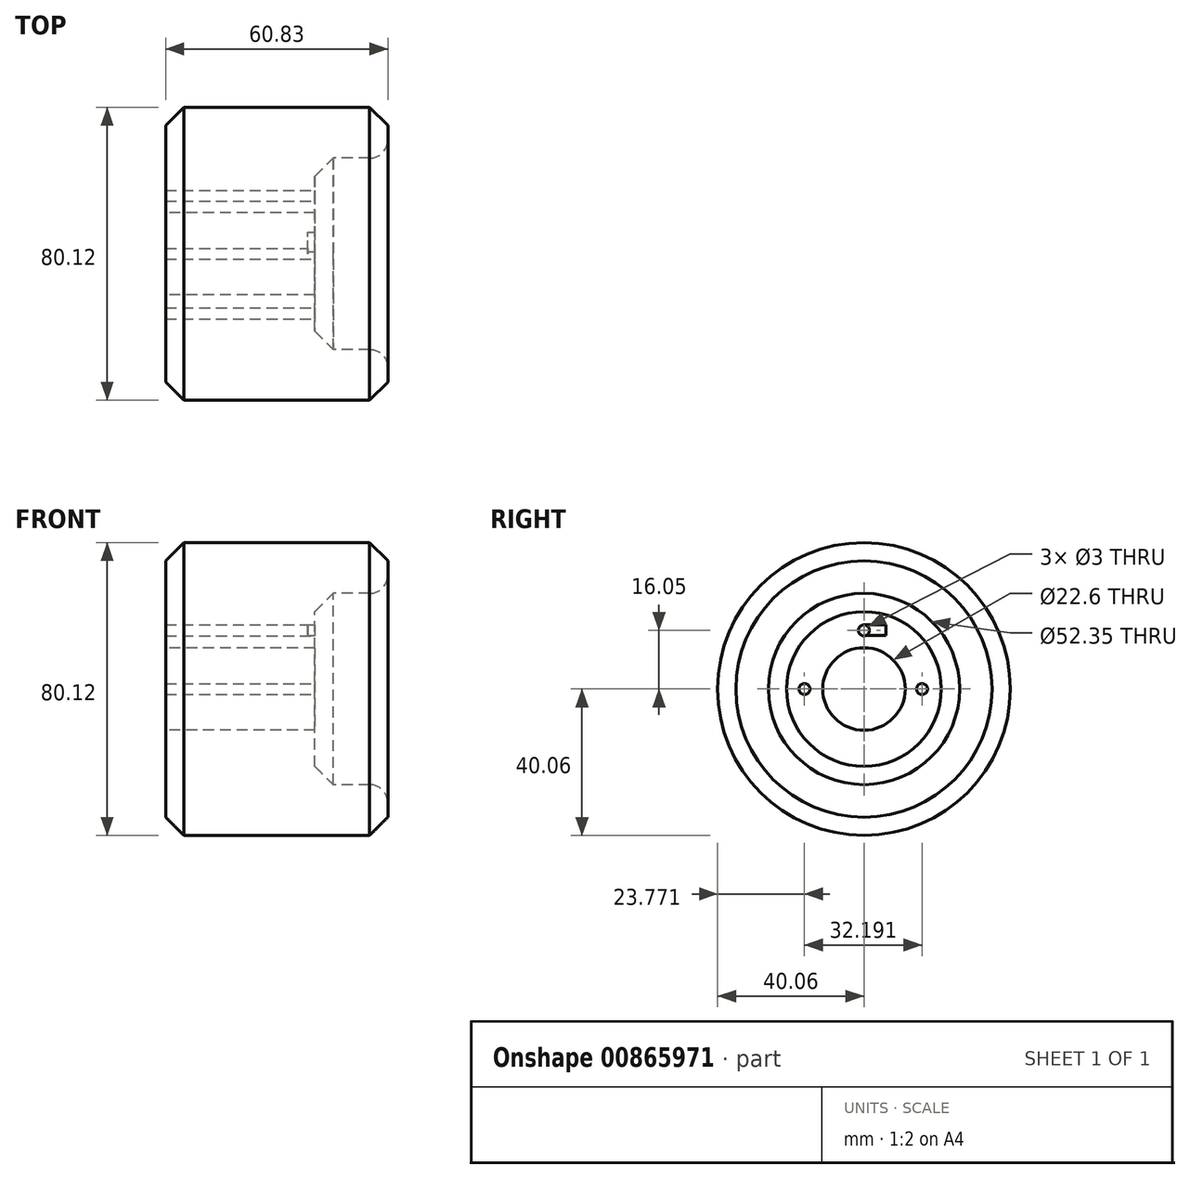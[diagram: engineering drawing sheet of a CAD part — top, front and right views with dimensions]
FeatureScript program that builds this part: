
annotation { "Feature Type Name" : "Feature", "Feature Type Description" : "" }
export const myFeature = defineFeature(function(context is Context, id is Id, definition is map)
    precondition{}
    {
        {
            var Q0;
            Q0=qCreatedBy(makeId("Front.planeOp"),FACE);
            var sketch = newSketch(context, id + "F0", { "sketchPlane" : qUnion([Q0])});
            skLineSegment(sketch, "E0", {"start": v(-75.38, 0) * mm, "end": v(58.63, 0) * mm, "construction": true});
            skLineSegment(sketch, "E1.bottom", {"start": v(-45.99, 40.06) * mm, "end": v(-5.14, 40.06) * mm});
            skLineSegment(sketch, "E1.top", {"start": v(-45.99, 11.3) * mm, "end": v(-5.14, 11.3) * mm});
            skLineSegment(sketch, "E1.left", {"start": v(-45.99, 40.06) * mm, "end": v(-45.99, 11.3) * mm});
            skLineSegment(sketch, "E1.right", {"start": v(-5.14, 40.06) * mm, "end": v(-5.14, 11.3) * mm});
            skLineSegment(sketch, "E2.bottom", {"start": v(-5.14, 40.06) * mm, "end": v(14.84, 40.06) * mm});
            skLineSegment(sketch, "E2.top", {"start": v(-5.14, 26.18) * mm, "end": v(14.84, 26.18) * mm});
            skLineSegment(sketch, "E2.left", {"start": v(-5.14, 40.06) * mm, "end": v(-5.14, 26.18) * mm});
            skLineSegment(sketch, "E2.right", {"start": v(14.84, 40.06) * mm, "end": v(14.84, 26.18) * mm});
            skSolve(sketch);
        }
        {
            var Q0;
            Q0=makeQuery(id+"F0.imprint","IMPRINT",FACE,{"disambiguationData":[TD([[makeQuery(id+"F0.imprint","IMPRINT",EDGE,{"derivedFrom":sQuery(id+"F0.wireOp",EDGE,"E1.bottom")}),-1.0]])]});
            var Q1;
            Q1=makeQuery(id+"F0.imprint","IMPRINT",FACE,{"disambiguationData":[TD([[makeQuery(id+"F0.imprint","IMPRINT",EDGE,{"derivedFrom":sQuery(id+"F0.wireOp",EDGE,"E2.bottom")}),-1.0]])]});
            var Q2;
            Q2=sQuery(id+"F0.wireOp",EDGE,"E0");
            revolve(context, id + "F1", {"surfaceOperationType" : NewSurfaceOperationType.NEW, "entities" : qUnion([Q0, Q1]), "axis" : qUnion([Q2]), "revolveType" : RevolveType.FULL});
        }
        {
            var Q0;
            Q0=makeQuery(id+"F1.opRevolve","SWEPT_EDGE",EDGE,{"disambiguationData":[OSD([sQuery(id+"F0.wireOp",EDGE,"E2.top"),sQuery(id+"F0.wireOp",EDGE,"E2.right")])]});
            fillet(context, id + "F2", {"entities" : qUnion([Q0]), "radius" : 5 * mm, "tangentPropagation" : true, "allowEdgeOverflow" : false});
        }
        {
            var Q0;
            Q0=makeQuery(id+"F1.opRevolve","SWEPT_EDGE",EDGE,{"disambiguationData":[OSD([sQuery(id+"F0.wireOp",EDGE,"E1.right"),sQuery(id+"F0.wireOp",EDGE,"E2.top"),sQuery(id+"F0.wireOp",EDGE,"E2.left")])]});
            var Q1;
            Q1=makeQuery(id+"F1.opRevolve","SWEPT_FACE",FACE,{"disambiguationData":[OSD([sQuery(id+"F0.wireOp",EDGE,"E1.bottom"),sQuery(id+"F0.wireOp",EDGE,"E2.bottom")])]});
            chamfer(context, id + "F3", {"entities" : qUnion([Q0, Q1]), "width" : 5 * mm, "tangentPropagation" : true});
        }
        {
            var Q0;
            Q0=makeQuery(id+"F1.opRevolve","SWEPT_FACE",FACE,{"disambiguationData":[OSD([sQuery(id+"F0.wireOp",EDGE,"E1.right")])]});
            var sketch = newSketch(context, id + "F4", { "sketchPlane" : qUnion([Q0])});
            skCircle(sketch, "E3", {"center": v(-16.29, 0) * mm, "radius": 2 * mm});
            skPoint(sketch, "E4", {"position": v(-21.18, 0) * mm});
            skPoint(sketch, "E5", {"position": v(-11.3, 0) * mm});
            skPoint(sketch, "E6", {"position": v(16.35, 0) * mm});
            skSolve(sketch);
        }
        {
            var Q0;
            Q0=sQuery(id+"F4.wireOp",VERTEX,"E3.center");
            var Q1;
            Q1=makeQuery(id+"F1.opRevolve","SWEPT_BODY",BODY,{"disambiguationData":[OSD([sQuery(id+"F0.wireOp",EDGE,"E1.bottom"),sQuery(id+"F0.wireOp",EDGE,"E1.top"),sQuery(id+"F0.wireOp",EDGE,"E1.left"),sQuery(id+"F0.wireOp",EDGE,"E1.right"),sQuery(id+"F0.wireOp",EDGE,"E2.bottom"),sQuery(id+"F0.wireOp",EDGE,"E2.top"),sQuery(id+"F0.wireOp",EDGE,"E2.right")])]});
            hole(context, id + "F5", {"style" : HoleStyle.SIMPLE, "endStyle" : HoleEndStyle.THROUGH, "holeDiameter" : 3 * mm, "majorDiameter" : 5 * mm, "isTappedThrough" : true, "tappedDepth" : 12 * mm, "tapClearance" : 3, "locations" : qUnion([Q0]), "scope" : qUnion([Q1])});
        }
        {
            var Q0;
            Q0=makeQuery(id+"F1.opRevolve","SWEPT_FACE",FACE,{"disambiguationData":[OSD([sQuery(id+"F0.wireOp",EDGE,"E1.right")])]});
            var sketch = newSketch(context, id + "F6", { "sketchPlane" : qUnion([Q0])});
            skPoint(sketch, "E7", {"position": v(15.9, 0) * mm});
            skSolve(sketch);
        }
        {
            var Q0;
            Q0=sQuery(id+"F6.wireOp",VERTEX,"E7");
            var Q1;
            Q1=makeQuery(id+"F1.opRevolve","SWEPT_BODY",BODY,{"disambiguationData":[OSD([sQuery(id+"F0.wireOp",EDGE,"E1.bottom"),sQuery(id+"F0.wireOp",EDGE,"E1.top"),sQuery(id+"F0.wireOp",EDGE,"E1.left"),sQuery(id+"F0.wireOp",EDGE,"E1.right"),sQuery(id+"F0.wireOp",EDGE,"E2.bottom"),sQuery(id+"F0.wireOp",EDGE,"E2.top"),sQuery(id+"F0.wireOp",EDGE,"E2.right")])]});
            hole(context, id + "F7", {"style" : HoleStyle.SIMPLE, "endStyle" : HoleEndStyle.THROUGH, "holeDiameter" : 3 * mm, "majorDiameter" : 5 * mm, "isTappedThrough" : true, "tappedDepth" : 12 * mm, "tapClearance" : 3, "locations" : qUnion([Q0]), "scope" : qUnion([Q1])});
        }
        {
            var Q0;
            Q0=makeQuery(id+"F1.opRevolve","SWEPT_FACE",FACE,{"disambiguationData":[OSD([sQuery(id+"F0.wireOp",EDGE,"E1.right")])]});
            var sketch = newSketch(context, id + "F8", { "sketchPlane" : qUnion([Q0])});
            skPoint(sketch, "E8", {"position": v(0, 16.05) * mm});
            skSolve(sketch);
        }
        {
            var Q0;
            Q0=sQuery(id+"F8.wireOp",VERTEX,"E8");
            var Q1;
            Q1=makeQuery(id+"F1.opRevolve","SWEPT_BODY",BODY,{"disambiguationData":[OSD([sQuery(id+"F0.wireOp",EDGE,"E1.bottom"),sQuery(id+"F0.wireOp",EDGE,"E1.top"),sQuery(id+"F0.wireOp",EDGE,"E1.left"),sQuery(id+"F0.wireOp",EDGE,"E1.right"),sQuery(id+"F0.wireOp",EDGE,"E2.bottom"),sQuery(id+"F0.wireOp",EDGE,"E2.top"),sQuery(id+"F0.wireOp",EDGE,"E2.right")])]});
            hole(context, id + "F9", {"style" : HoleStyle.SIMPLE, "endStyle" : HoleEndStyle.THROUGH, "holeDiameter" : 3 * mm, "majorDiameter" : 5 * mm, "isTappedThrough" : true, "tappedDepth" : 12 * mm, "tapClearance" : 3, "locations" : qUnion([Q0]), "scope" : qUnion([Q1])});
        }
        {
            var Q0;
            Q0=makeQuery(id+"F1.opRevolve","SWEPT_FACE",FACE,{"disambiguationData":[OSD([sQuery(id+"F0.wireOp",EDGE,"E1.right")])]});
            var sketch = newSketch(context, id + "F10", { "sketchPlane" : qUnion([Q0])});
            skLineSegment(sketch, "E9.bottom", {"start": v(0, 17.55) * mm, "end": v(5.97, 17.55) * mm});
            skLineSegment(sketch, "E9.top", {"start": v(0, 14.66) * mm, "end": v(5.97, 14.66) * mm});
            skLineSegment(sketch, "E9.left", {"start": v(0, 17.55) * mm, "end": v(0, 14.66) * mm});
            skLineSegment(sketch, "E9.right", {"start": v(5.97, 17.55) * mm, "end": v(5.97, 14.66) * mm});
            skSolve(sketch);
        }
        {
            var Q0;
            {var subQ0=sQuery(id+"F10.wireOp",EDGE,"E9.bottom");Q0=makeQuery(id+"F10.imprint","IMPRINT",FACE,{"disambiguationData":[TD([[makeQuery(id+"F10.imprint","IMPRINT",EDGE,{"derivedFrom":subQ0}),-1.0]])]});}
            extrude(context, id + "F11", {"entities" : qUnion([Q0]), "operationType" : NewBodyOperationType.REMOVE, "oppositeDirection" : true, "depth" : 2 * mm, "offsetDistance" : 25 * mm});
        }
    });
